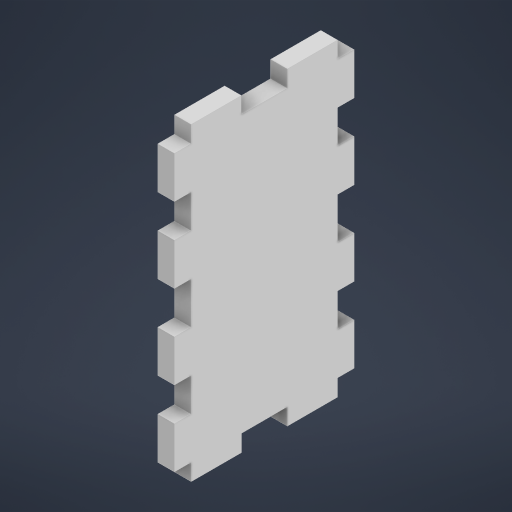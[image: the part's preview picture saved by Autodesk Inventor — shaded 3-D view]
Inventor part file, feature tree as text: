
AUTODESK INVENTOR PART (.ipt)
format: ipt  version: 2023.2 (Build 272271000, 271)  size: 336,896 bytes
history: native  units: mm
features: sketch x2, extrude x1
ambient origin geometry x8: Origin, YZ Plane, XZ Plane, XY Plane, X Axis, Y Axis, Z Axis, Center Point
bodies: Body1 (feature_tree)
feature tree (3):
  extrude  "Extrusion17"  Depth=43.0mm
  sketch  "Sketch1"  dims[d228=74.0mm d229=43.0mm]
  sketch  "Sketch15"  dims[d230=4.0mm d231=0.0mm d232=4.0mm d233=12.0mm d234=10.0mm d246=10.0mm d248=8.0mm d250=10.0mm d251=4.0mm d252=0.0mm d9=0.5mm d10=0.872665mm d11=0.5mm d12=0.872665mm d13=0.5mm d14=0.872665mm d27=0.5mm d28=0.872665mm d29=0.5mm d30=0.872665mm d88=0.5mm d89=0.872665mm d90=0.5mm d91=0.872665mm d116=0.5mm d117=0.872665mm d118=0.5mm d119=0.872665mm d154=0.5mm d155=0.872665mm d156=0.5mm d157=0.872665mm d181=0.5mm d182=0.872665mm d183=0.5mm d184=0.872665mm d221=0.5mm d222=0.872665mm d223=0.5mm d224=0.872665mm]
